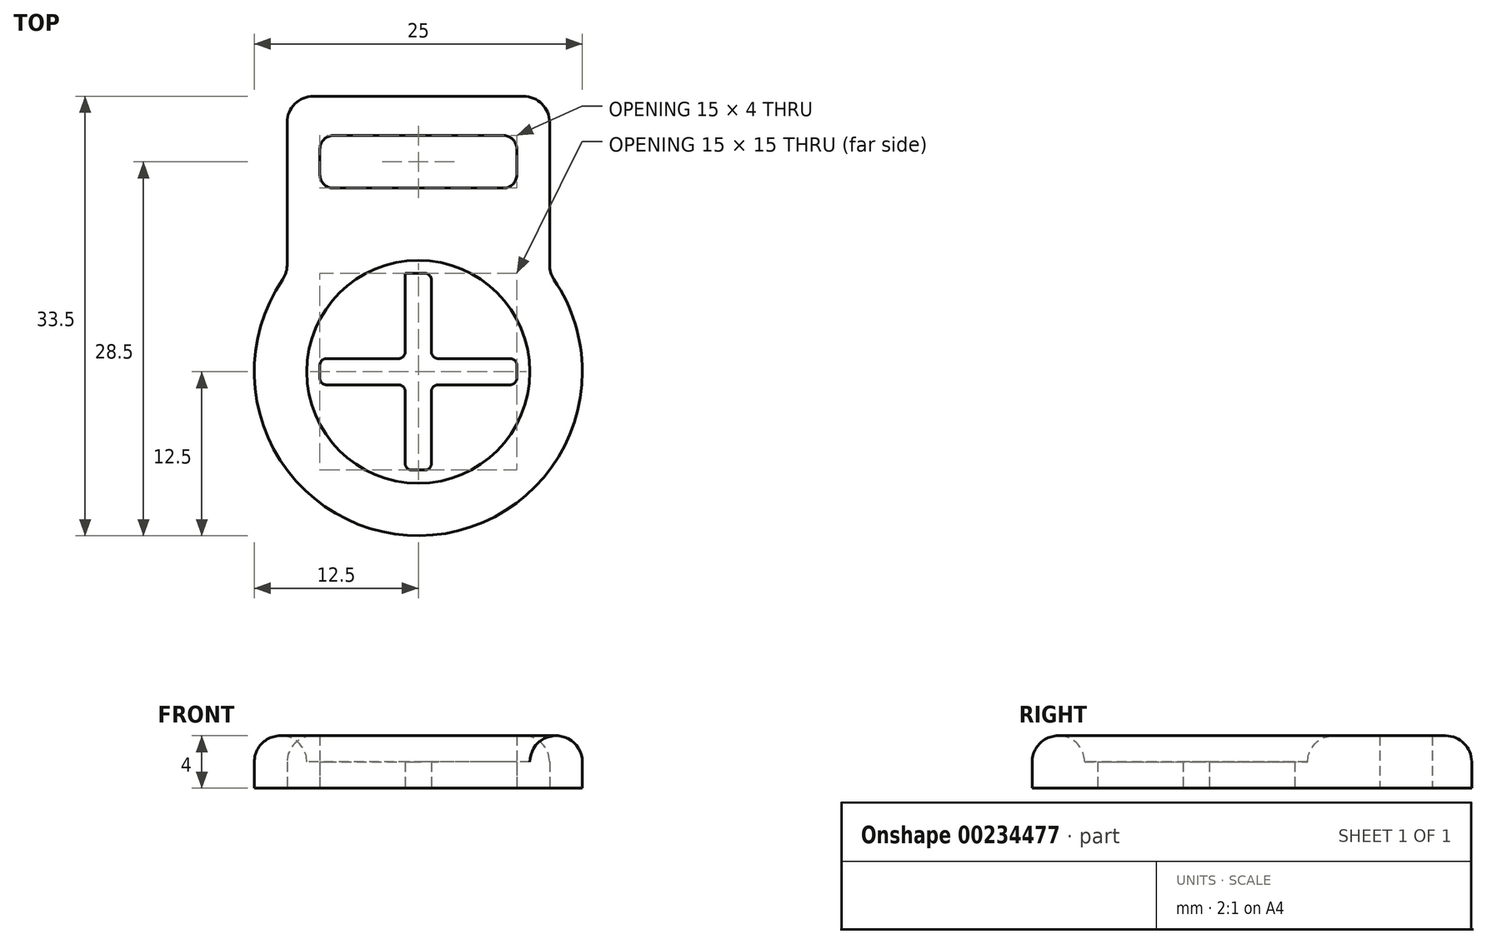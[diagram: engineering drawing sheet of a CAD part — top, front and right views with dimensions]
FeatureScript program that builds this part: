
annotation { "Feature Type Name" : "Feature", "Feature Type Description" : "" }
export const myFeature = defineFeature(function(context is Context, id is Id, definition is map)
    precondition{}
    {
        {
            var Q0;
            Q0=qCreatedBy(makeId("Top.planeOp"),FACE);
            var sketch = newSketch(context, id + "F0", { "sketchPlane" : qUnion([Q0])});
            skArc(sketch, "E0", {"start": v(-10, 7.5) * mm, "mid": v(0, -12.5) * mm, "end": v(10, 7.5) * mm});
            skCircle(sketch, "E1", {"center": v(0, 0) * mm, "radius": 8.5 * mm});
            skLineSegment(sketch, "E2", {"start": v(-10, 7.5) * mm, "end": v(-10, 21) * mm});
            skLineSegment(sketch, "E3", {"start": v(-10, 21) * mm, "end": v(10, 21) * mm});
            skLineSegment(sketch, "E4", {"start": v(10, 21) * mm, "end": v(10, 7.5) * mm});
            skLineSegment(sketch, "E5.bottom", {"start": v(-7.5, 18) * mm, "end": v(7.5, 18) * mm});
            skLineSegment(sketch, "E5.top", {"start": v(-7.5, 14) * mm, "end": v(7.5, 14) * mm});
            skLineSegment(sketch, "E5.left", {"start": v(-7.5, 18) * mm, "end": v(-7.5, 14) * mm});
            skLineSegment(sketch, "E5.right", {"start": v(7.5, 18) * mm, "end": v(7.5, 14) * mm});
            skSolve(sketch);
        }
        {
            var Q0;
            Q0 = qSketchRegion(id + "F0", true);
            extrude(context, id + "F1", {"entities" : qUnion([Q0]), "depth" : 4 * mm, "offsetDistance" : 25 * mm});
        }
        {
            var Q0;
            Q0=qCreatedBy(makeId("Top.planeOp"),FACE);
            var sketch = newSketch(context, id + "F2", { "sketchPlane" : qUnion([Q0])});
            skCircle(sketch, "E6.0", {"center": v(0, 0) * mm, "radius": 8.5 * mm});
            skLineSegment(sketch, "E7", {"start": v(7.5, 1) * mm, "end": v(1, 1) * mm});
            skLineSegment(sketch, "E8", {"start": v(1, 1) * mm, "end": v(1, 7.5) * mm});
            skLineSegment(sketch, "E9", {"start": v(1, 7.5) * mm, "end": v(-1, 7.5) * mm});
            skLineSegment(sketch, "E10", {"start": v(-1, 7.5) * mm, "end": v(-1, 1) * mm});
            skLineSegment(sketch, "E11", {"start": v(-1, 1) * mm, "end": v(-7.5, 1) * mm});
            skLineSegment(sketch, "E12", {"start": v(-7.5, 1) * mm, "end": v(-7.5, -1) * mm});
            skLineSegment(sketch, "E13", {"start": v(-7.5, -1) * mm, "end": v(-1, -1) * mm});
            skLineSegment(sketch, "E14", {"start": v(-1, -1) * mm, "end": v(-1, -7.5) * mm});
            skLineSegment(sketch, "E15", {"start": v(-1, -7.5) * mm, "end": v(1, -7.5) * mm});
            skLineSegment(sketch, "E16", {"start": v(1, -7.5) * mm, "end": v(1, -1) * mm});
            skLineSegment(sketch, "E17", {"start": v(1, -1) * mm, "end": v(7.5, -1) * mm});
            skLineSegment(sketch, "E18", {"start": v(7.5, -1) * mm, "end": v(7.5, 1) * mm});
            skSolve(sketch);
        }
        {
            var Q0;
            Q0 = qSketchRegion(id + "F2", true);
            extrude(context, id + "F3", {"entities" : qUnion([Q0]), "operationType" : NewBodyOperationType.ADD, "depth" : 2 * mm, "offsetDistance" : 25 * mm});
        }
        {
            var Q0;
            Q0=makeQuery(id+"F1.opExtrude","SWEPT_EDGE",EDGE,{"disambiguationData":[OSD([sQuery(id+"F0.wireOp",EDGE,"E2"),sQuery(id+"F0.wireOp",EDGE,"E3")])]});
            var Q1;
            Q1=makeQuery(id+"F1.opExtrude","SWEPT_EDGE",EDGE,{"disambiguationData":[OSD([sQuery(id+"F0.wireOp",EDGE,"E3"),sQuery(id+"F0.wireOp",EDGE,"E4")])]});
            var Q2;
            Q2=makeQuery(id+"F1.opExtrude","SWEPT_EDGE",EDGE,{"disambiguationData":[OSD([sQuery(id+"F0.wireOp",EDGE,"E0"),sQuery(id+"F0.wireOp",EDGE,"E2")])]});
            var Q3;
            Q3=makeQuery(id+"F1.opExtrude","SWEPT_EDGE",EDGE,{"disambiguationData":[OSD([sQuery(id+"F0.wireOp",EDGE,"E0"),sQuery(id+"F0.wireOp",EDGE,"E4")])]});
            fillet(context, id + "F4", {"entities" : qUnion([Q0, Q1, Q2, Q3]), "tangentPropagation" : true, "radius" : 2 * mm, "defaultsChanged" : false, "vertexSettings" : [], "allowEdgeOverflow" : false});
        }
        {
            var Q0;
            Q0=makeQuery(id+"F1.opExtrude","SWEPT_EDGE",EDGE,{"disambiguationData":[OSD([sQuery(id+"F0.wireOp",EDGE,"E5.bottom"),sQuery(id+"F0.wireOp",EDGE,"E5.right")])]});
            var Q1;
            Q1=makeQuery(id+"F1.opExtrude","SWEPT_EDGE",EDGE,{"disambiguationData":[OSD([sQuery(id+"F0.wireOp",EDGE,"E5.top"),sQuery(id+"F0.wireOp",EDGE,"E5.right")])]});
            var Q2;
            Q2=makeQuery(id+"F1.opExtrude","SWEPT_EDGE",EDGE,{"disambiguationData":[OSD([sQuery(id+"F0.wireOp",EDGE,"E5.bottom"),sQuery(id+"F0.wireOp",EDGE,"E5.left")])]});
            var Q3;
            Q3=makeQuery(id+"F1.opExtrude","SWEPT_EDGE",EDGE,{"disambiguationData":[OSD([sQuery(id+"F0.wireOp",EDGE,"E5.top"),sQuery(id+"F0.wireOp",EDGE,"E5.left")])]});
            fillet(context, id + "F5", {"entities" : qUnion([Q0, Q1, Q2, Q3]), "tangentPropagation" : true, "radius" : 1 * mm, "defaultsChanged" : false, "vertexSettings" : [], "allowEdgeOverflow" : false});
        }
        {
            var Q0;
            Q0=makeQuery(id+"F1.opExtrude","CAP_EDGE",EDGE,{"disambiguationData":[OSD([sQuery(id+"F0.wireOp",EDGE,"E0")])],"isStart":false});
            var Q1;
            Q1=makeQuery(id+"F1.opExtrude","CAP_EDGE",EDGE,{"disambiguationData":[OSD([sQuery(id+"F0.wireOp",EDGE,"E1")])],"isStart":false});
            fillet(context, id + "F6", {"entities" : qUnion([Q0, Q1]), "tangentPropagation" : true, "radius" : 2 * mm, "defaultsChanged" : true, "vertexSettings" : [], "allowEdgeOverflow" : false});
        }
        {
            var Q0;
            Q0=makeQuery(id+"F3.opExtrude","SWEPT_EDGE",EDGE,{"disambiguationData":[OSD([sQuery(id+"F2.wireOp",EDGE,"E7"),sQuery(id+"F2.wireOp",EDGE,"E18")])]});
            var Q1;
            Q1=makeQuery(id+"F3.opExtrude","SWEPT_EDGE",EDGE,{"disambiguationData":[OSD([sQuery(id+"F2.wireOp",EDGE,"E8"),sQuery(id+"F2.wireOp",EDGE,"E9")])]});
            var Q2;
            Q2=makeQuery(id+"F3.opExtrude","SWEPT_EDGE",EDGE,{"disambiguationData":[OSD([sQuery(id+"F2.wireOp",EDGE,"E7"),sQuery(id+"F2.wireOp",EDGE,"E8")])]});
            var Q3;
            Q3=makeQuery(id+"F3.opExtrude","SWEPT_EDGE",EDGE,{"disambiguationData":[OSD([sQuery(id+"F2.wireOp",EDGE,"E16"),sQuery(id+"F2.wireOp",EDGE,"E17")])]});
            var Q4;
            Q4=makeQuery(id+"F3.opExtrude","SWEPT_EDGE",EDGE,{"disambiguationData":[OSD([sQuery(id+"F2.wireOp",EDGE,"E10"),sQuery(id+"F2.wireOp",EDGE,"E11")])]});
            var Q5;
            Q5=makeQuery(id+"F3.opExtrude","SWEPT_EDGE",EDGE,{"disambiguationData":[OSD([sQuery(id+"F2.wireOp",EDGE,"E15"),sQuery(id+"F2.wireOp",EDGE,"E16")])]});
            var Q6;
            Q6=makeQuery(id+"F3.opExtrude","SWEPT_EDGE",EDGE,{"disambiguationData":[OSD([sQuery(id+"F2.wireOp",EDGE,"E17"),sQuery(id+"F2.wireOp",EDGE,"E18")])]});
            var Q7;
            Q7=makeQuery(id+"F3.opExtrude","SWEPT_EDGE",EDGE,{"disambiguationData":[OSD([sQuery(id+"F2.wireOp",EDGE,"E12"),sQuery(id+"F2.wireOp",EDGE,"E13")])]});
            var Q8;
            Q8=makeQuery(id+"F3.opExtrude","SWEPT_EDGE",EDGE,{"disambiguationData":[OSD([sQuery(id+"F2.wireOp",EDGE,"E13"),sQuery(id+"F2.wireOp",EDGE,"E14")])]});
            var Q9;
            Q9=makeQuery(id+"F3.opExtrude","SWEPT_EDGE",EDGE,{"disambiguationData":[OSD([sQuery(id+"F2.wireOp",EDGE,"E14"),sQuery(id+"F2.wireOp",EDGE,"E15")])]});
            var Q10;
            Q10=makeQuery(id+"F3.opExtrude","SWEPT_EDGE",EDGE,{"disambiguationData":[OSD([sQuery(id+"F2.wireOp",EDGE,"E11"),sQuery(id+"F2.wireOp",EDGE,"E12")])]});
            fillet(context, id + "F7", {"entities" : qUnion([Q0, Q1, Q2, Q3, Q4, Q5, Q6, Q7, Q8, Q9, Q10]), "tangentPropagation" : true, "radius" : 0.5 * mm, "defaultsChanged" : false, "vertexSettings" : [], "allowEdgeOverflow" : false});
        }
    });
